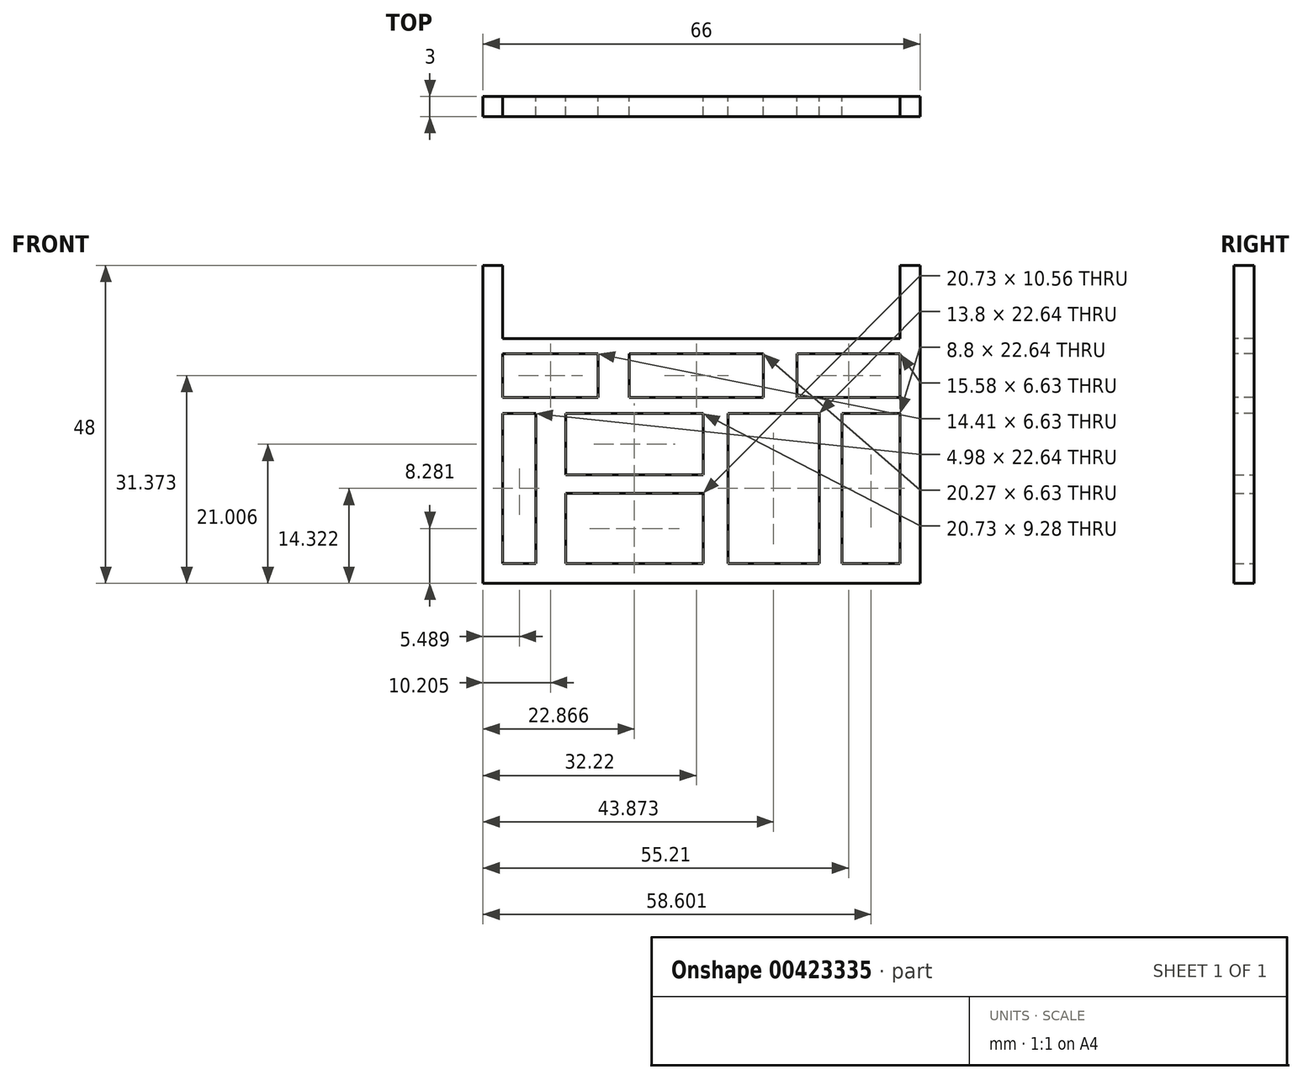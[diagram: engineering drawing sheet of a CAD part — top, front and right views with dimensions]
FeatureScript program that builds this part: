
annotation { "Feature Type Name" : "Feature", "Feature Type Description" : "" }
export const myFeature = defineFeature(function(context is Context, id is Id, definition is map)
    precondition{}
    {
        {
            var Q0;
            Q0=qCreatedBy(makeId("Front.planeOp"),FACE);
            var sketch = newSketch(context, id + "F0", { "sketchPlane" : qUnion([Q0])});
            skLineSegment(sketch, "E0.bottom", {"start": v(0, 0) * mm, "end": v(60, 0) * mm});
            skLineSegment(sketch, "E0.left", {"start": v(0, 0) * mm, "end": v(0, 45) * mm});
            skLineSegment(sketch, "E0.right", {"start": v(60, 0) * mm, "end": v(60, 45) * mm});
            skLineSegment(sketch, "E1.0", {"start": v(-3, -3) * mm, "end": v(-3, 45) * mm});
            skLineSegment(sketch, "E1.1", {"start": v(-3, -3) * mm, "end": v(63, -3) * mm});
            skLineSegment(sketch, "E1.2", {"start": v(63, -3) * mm, "end": v(63, 45) * mm});
            skLineSegment(sketch, "E2", {"start": v(-3, 45) * mm, "end": v(0, 45) * mm});
            skLineSegment(sketch, "E3", {"start": v(60, 45) * mm, "end": v(63, 45) * mm});
            skSolve(sketch);
        }
        {
            var Q0;
            Q0 = qSketchRegion(id + "F0", true);
            extrude(context, id + "F1", {"entities" : qUnion([Q0]), "depth" : 60 * mm});
        }
        {
            var Q0;
            Q0=qCreatedBy(makeId("Front.planeOp"),FACE);
            var sketch = newSketch(context, id + "F2", { "sketchPlane" : qUnion([Q0])});
            skLineSegment(sketch, "E4.bottom", {"start": v(60.87, 33.95) * mm, "end": v(-0.95, 33.95) * mm});
            skLineSegment(sketch, "E4.top", {"start": v(60.87, 31.69) * mm, "end": v(-0.95, 31.69) * mm});
            skLineSegment(sketch, "E4.left", {"start": v(60.87, 33.95) * mm, "end": v(60.87, 31.69) * mm});
            skLineSegment(sketch, "E4.right", {"start": v(-0.95, 33.95) * mm, "end": v(-0.95, 31.69) * mm});
            skLineSegment(sketch, "E5.bottom", {"start": v(62.04, 25.06) * mm, "end": v(-2.2, 25.06) * mm});
            skLineSegment(sketch, "E5.top", {"start": v(62.04, 22.64) * mm, "end": v(-2.2, 22.64) * mm});
            skLineSegment(sketch, "E5.left", {"start": v(62.04, 25.06) * mm, "end": v(62.04, 22.64) * mm});
            skLineSegment(sketch, "E5.right", {"start": v(-2.2, 25.06) * mm, "end": v(-2.2, 22.64) * mm});
            skLineSegment(sketch, "E6.bottom", {"start": v(51.2, 23.5) * mm, "end": v(47.77, 23.5) * mm});
            skLineSegment(sketch, "E6.top", {"start": v(51.2, -1.2) * mm, "end": v(47.77, -1.2) * mm});
            skLineSegment(sketch, "E6.left", {"start": v(51.2, 23.5) * mm, "end": v(51.2, -1.2) * mm});
            skLineSegment(sketch, "E6.right", {"start": v(47.77, 23.5) * mm, "end": v(47.77, -1.2) * mm});
            skLineSegment(sketch, "E7.bottom", {"start": v(33.97, 23.5) * mm, "end": v(30.23, 23.5) * mm});
            skLineSegment(sketch, "E7.top", {"start": v(33.97, -1.2) * mm, "end": v(30.23, -1.2) * mm});
            skLineSegment(sketch, "E7.left", {"start": v(33.97, 23.5) * mm, "end": v(33.97, -1.2) * mm});
            skLineSegment(sketch, "E7.right", {"start": v(30.23, 23.5) * mm, "end": v(30.23, -1.2) * mm});
            skLineSegment(sketch, "E8.bottom", {"start": v(19.09, 32.93) * mm, "end": v(14.4, 32.93) * mm});
            skLineSegment(sketch, "E8.top", {"start": v(19.09, 23.66) * mm, "end": v(14.4, 23.66) * mm});
            skLineSegment(sketch, "E8.left", {"start": v(19.09, 32.93) * mm, "end": v(19.09, 23.66) * mm});
            skLineSegment(sketch, "E8.right", {"start": v(14.4, 32.93) * mm, "end": v(14.4, 23.66) * mm});
            skLineSegment(sketch, "E9.bottom", {"start": v(44.42, 32.7) * mm, "end": v(39.35, 32.7) * mm});
            skLineSegment(sketch, "E9.top", {"start": v(44.42, 23.66) * mm, "end": v(39.35, 23.66) * mm});
            skLineSegment(sketch, "E9.left", {"start": v(44.42, 32.7) * mm, "end": v(44.42, 23.66) * mm});
            skLineSegment(sketch, "E9.right", {"start": v(39.35, 32.7) * mm, "end": v(39.35, 23.66) * mm});
            skLineSegment(sketch, "E10.bottom", {"start": v(9.5, 23.66) * mm, "end": v(4.98, 23.66) * mm});
            skLineSegment(sketch, "E10.top", {"start": v(9.5, -1.2) * mm, "end": v(4.98, -1.2) * mm});
            skLineSegment(sketch, "E10.left", {"start": v(9.5, 23.66) * mm, "end": v(9.5, -1.2) * mm});
            skLineSegment(sketch, "E10.right", {"start": v(4.98, 23.66) * mm, "end": v(4.98, -1.2) * mm});
            skLineSegment(sketch, "E11.bottom", {"start": v(31.64, 13.37) * mm, "end": v(8.33, 13.37) * mm});
            skLineSegment(sketch, "E11.top", {"start": v(31.64, 10.56) * mm, "end": v(8.33, 10.56) * mm});
            skLineSegment(sketch, "E11.left", {"start": v(31.64, 13.37) * mm, "end": v(31.64, 10.56) * mm});
            skLineSegment(sketch, "E11.right", {"start": v(8.33, 13.37) * mm, "end": v(8.33, 10.56) * mm});
            skSolve(sketch);
        }
        {
            var Q0;
            Q0 = qSketchRegion(id + "F2", true);
            extrude(context, id + "F3", {"entities" : qUnion([Q0]), "operationType" : NewBodyOperationType.ADD, "depth" : 3 * mm});
        }
        {
            var Q0;
            Q0=makeQuery(id+"F1.opExtrude","CAP_FACE",FACE,{"disambiguationData":[OSD([sQuery(id+"F0.wireOp",EDGE,"E0.bottom"),sQuery(id+"F0.wireOp",EDGE,"E0.left"),sQuery(id+"F0.wireOp",EDGE,"E0.right"),sQuery(id+"F0.wireOp",EDGE,"E1.0"),sQuery(id+"F0.wireOp",EDGE,"E1.1"),sQuery(id+"F0.wireOp",EDGE,"E1.2"),sQuery(id+"F0.wireOp",EDGE,"E2"),sQuery(id+"F0.wireOp",EDGE,"E3")])],"isStart":false});
            var sketch = newSketch(context, id + "F4", { "sketchPlane" : qUnion([Q0])});
            skLineSegment(sketch, "E12.bottom", {"start": v(-19.26, 58) * mm, "end": v(86.85, 58) * mm});
            skLineSegment(sketch, "E12.top", {"start": v(-19.26, -16.43) * mm, "end": v(86.85, -16.43) * mm});
            skLineSegment(sketch, "E12.left", {"start": v(-19.26, 58) * mm, "end": v(-19.26, -16.43) * mm});
            skLineSegment(sketch, "E12.right", {"start": v(86.85, 58) * mm, "end": v(86.85, -16.43) * mm});
            skSolve(sketch);
        }
        {
            var Q0;
            Q0 = qSketchRegion(id + "F4", true);
            var Q1;
            Q1=makeQuery(id+"F3.opExtrude","CAP_FACE",FACE,{"disambiguationData":[OSD([sQuery(id+"F2.wireOp",EDGE,"E4.bottom"),sQuery(id+"F2.wireOp",EDGE,"E4.top"),sQuery(id+"F2.wireOp",EDGE,"E4.left"),sQuery(id+"F2.wireOp",EDGE,"E4.right"),sQuery(id+"F2.wireOp",EDGE,"E5.bottom"),sQuery(id+"F2.wireOp",EDGE,"E5.top"),sQuery(id+"F2.wireOp",EDGE,"E5.left"),sQuery(id+"F2.wireOp",EDGE,"E5.right"),sQuery(id+"F2.wireOp",EDGE,"E6.top"),sQuery(id+"F2.wireOp",EDGE,"E6.left"),sQuery(id+"F2.wireOp",EDGE,"E6.right"),sQuery(id+"F2.wireOp",EDGE,"E7.top"),sQuery(id+"F2.wireOp",EDGE,"E7.left"),sQuery(id+"F2.wireOp",EDGE,"E7.right"),sQuery(id+"F2.wireOp",EDGE,"E8.left"),sQuery(id+"F2.wireOp",EDGE,"E8.right"),sQuery(id+"F2.wireOp",EDGE,"E9.left"),sQuery(id+"F2.wireOp",EDGE,"E9.right"),sQuery(id+"F2.wireOp",EDGE,"E10.top"),sQuery(id+"F2.wireOp",EDGE,"E10.left"),sQuery(id+"F2.wireOp",EDGE,"E10.right"),sQuery(id+"F2.wireOp",EDGE,"E11.bottom"),sQuery(id+"F2.wireOp",EDGE,"E11.top")])],"isStart":false});
            extrude(context, id + "F5", {"entities" : qUnion([Q0]), "operationType" : NewBodyOperationType.REMOVE, "endBound" : BoundingType.UP_TO_SURFACE, "oppositeDirection" : true, "endBoundEntityFace" : qUnion([Q1]), "depth" : 25 * mm});
        }
    });
